# Revit family: 0044001 Sylvania Lighting Fixture OptiClip 600 4000K C8 WH DALI WHITE
name_source: partatom
category: Lighting Fixtures
revit_build: Autodesk Revit 2016 (Build: 20150220_1215(x64)
units: mm (PartAtom-declared; Revit-internal decimal feet)

## family parameters
Cut with Voids When Loaded = No
Host = Face
Light Source = Yes
OmniClass Number = 23.80.70.00
OmniClass Title = Lighting
Part Type = Normal
Room Calculation Point = No
Round Connector Dimension = Use Diameter
Shared = No

## types (1)
- Type Name
    Apparent Load = 0 VA
    Assembly Code = D5020200
    ClassificationName = Uniclass2015
    ClassificationValue = EF_70_80
    Color Filter = 16777215
    Cost = 0 $
    Default Elevation = 1219 mm
    Dimming Lamp Color Temperature Shift = <None>
    DurationUnit = hours
    Emit Shape Visible in Rendering = No
    Emit from Circle Diameter = 610 mm
    ExpectedLife = 50000
    Height = 50 mm  [stored 0.164042 ft]
    IfcExportAs = IfcLightFixtureType
    IfcExportType = IfcLightFixtureType
    Keynote = 16500
    Length = 595 mm  [stored 1.9521 ft]
    Manufacturer = Feilo Sylvania
    ManufacturerName = Feilo Sylvania
    Material_1_FEILO = <By Category>
    Material_2_FEILO = <By Category>
    Material_3_FEILO = <By Category>
    Material_4_FEILO = <By Category>
    NominalDepth = 0 mm  [stored 0 ft]
    NominalHeight = 0 mm  [stored 0 ft]
    NominalLength = 0 mm  [stored 0 ft]
    Photometric Web File = 0044001.ies
    PowerFactor = 0
    Tilt Angle = 90.00°
    Type Image = <None>
    URL = http://www.feilosylvania.com
    Voltage = 0 V
    Width = 595 mm  [stored 1.9521 ft]
    cut out length = 590 mm  [stored 1.9357 ft]
    cut out width = 590 mm  [stored 1.9357 ft]
    height = 15 mm
    spacer centres = 1000 mm  [stored 3.28084 ft]
    spacer height = 5 mm  [stored 0.0164042 ft]

note: [stored X ft] marks values corroborated as IEEE doubles in the binary element streams (Revit-internal decimal feet)

## geometry (parser evidence)
native form markers: Sweep x2
no freeform markers — native parametric forms only
